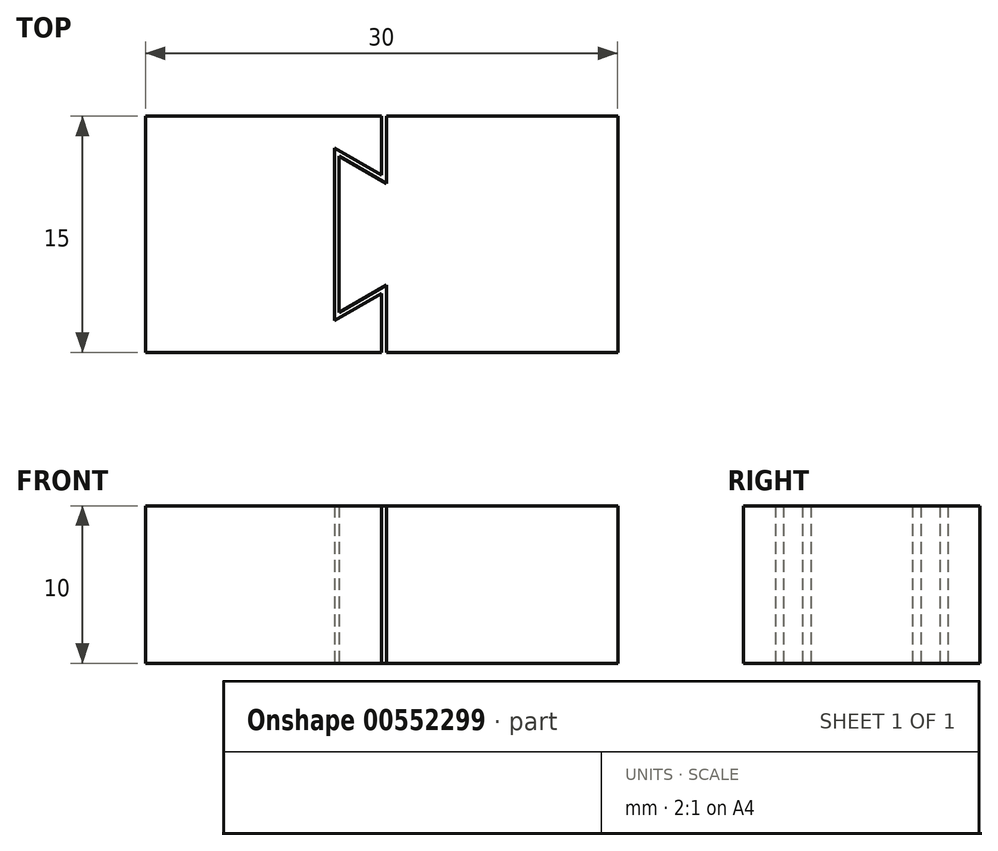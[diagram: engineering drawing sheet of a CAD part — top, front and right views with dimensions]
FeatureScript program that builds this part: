
annotation { "Feature Type Name" : "Feature", "Feature Type Description" : "" }
export const myFeature = defineFeature(function(context is Context, id is Id, definition is map)
    precondition{}
    {
        {
            var Q0;
            Q0=qCreatedBy(makeId("Top.planeOp"),FACE);
            var sketch = newSketch(context, id + "F0", { "sketchPlane" : qUnion([Q0])});
            skLineSegment(sketch, "E0.bottom", {"start": v(-5.64, 11.1) * mm, "end": v(24.36, 11.1) * mm});
            skLineSegment(sketch, "E0.top", {"start": v(-5.64, -3.9) * mm, "end": v(24.36, -3.9) * mm});
            skLineSegment(sketch, "E0.left", {"start": v(-5.64, 11.1) * mm, "end": v(-5.64, -3.9) * mm});
            skLineSegment(sketch, "E0.right", {"start": v(24.36, 11.1) * mm, "end": v(24.36, -3.9) * mm});
            skLineSegment(sketch, "E1", {"start": v(-5.64, 3.6) * mm, "end": v(24.36, 3.6) * mm, "construction": true});
            skLineSegment(sketch, "E2", {"start": v(9.36, 7.36) * mm, "end": v(9.36, 11.1) * mm});
            skLineSegment(sketch, "E3", {"start": v(9.36, 7.36) * mm, "end": v(6.36, 9.09) * mm});
            skLineSegment(sketch, "E4", {"start": v(6.36, 9.09) * mm, "end": v(6.36, 3.6) * mm});
            skPoint(sketch, "E5.orphan", {"position": v(9.36, 3.6) * mm});
            skLineSegment(sketch, "E6.MirrorCS", {"start": v(6.36, -1.88) * mm, "end": v(6.36, 3.6) * mm});
            skLineSegment(sketch, "E7.MirrorCS", {"start": v(9.36, -0.14) * mm, "end": v(6.36, -1.88) * mm});
            skLineSegment(sketch, "E8.MirrorCS", {"start": v(9.36, -0.14) * mm, "end": v(9.36, -3.9) * mm});
            skLineSegment(sketch, "E9.0", {"start": v(9.66, 0.38) * mm, "end": v(9.66, -3.9) * mm});
            skLineSegment(sketch, "E9.1", {"start": v(9.66, 0.38) * mm, "end": v(6.66, -1.36) * mm});
            skLineSegment(sketch, "E9.2", {"start": v(9.66, 6.84) * mm, "end": v(9.66, 11.1) * mm});
            skLineSegment(sketch, "E9.3", {"start": v(9.66, 6.84) * mm, "end": v(6.66, 8.57) * mm});
            skLineSegment(sketch, "E9.4", {"start": v(6.66, 8.57) * mm, "end": v(6.66, 3.6) * mm});
            skLineSegment(sketch, "E9.5", {"start": v(6.66, -1.36) * mm, "end": v(6.66, 3.6) * mm});
            skSolve(sketch);
        }
        {
            var Q0;
            {var subQ1=sQuery(id+"F0.wireOp",EDGE,"E0.left");Q0=makeQuery(id+"F0.imprint","IMPRINT",FACE,{"disambiguationData":[TD([[makeQuery(id+"F0.imprint","IMPRINT",EDGE,{"derivedFrom":subQ1}),1.0]])]});}
            extrude(context, id + "F1", {"entities" : qUnion([Q0]), "depth" : 10 * mm, "offsetDistance" : 25 * mm});
        }
        {
            var Q0;
            {var subQ1=sQuery(id+"F0.wireOp",EDGE,"E0.right");Q0=makeQuery(id+"F0.imprint","IMPRINT",FACE,{"disambiguationData":[TD([[makeQuery(id+"F0.imprint","IMPRINT",EDGE,{"derivedFrom":subQ1}),-1.0]])]});}
            extrude(context, id + "F2", {"entities" : qUnion([Q0]), "depth" : 10 * mm, "offsetDistance" : 25 * mm});
        }
    });
